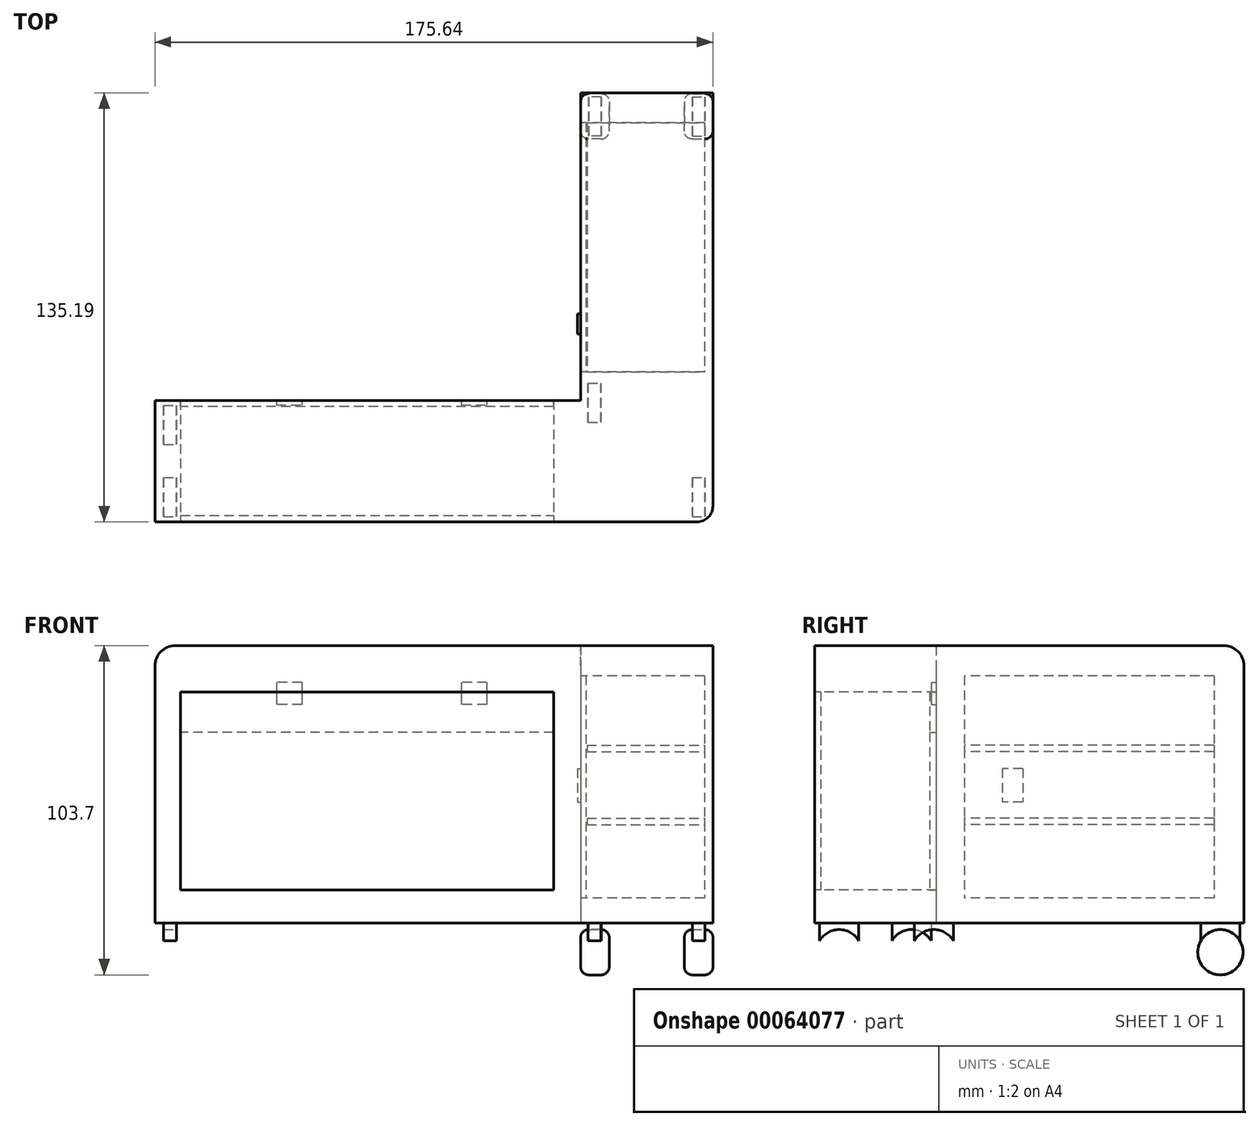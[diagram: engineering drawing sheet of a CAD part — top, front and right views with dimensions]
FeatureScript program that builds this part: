
annotation { "Feature Type Name" : "Feature", "Feature Type Description" : "" }
export const myFeature = defineFeature(function(context is Context, id is Id, definition is map)
    precondition{}
    {
        {
            var Q0;
            Q0=qCreatedBy(makeId("Front.planeOp"),FACE);
            var sketch = newSketch(context, id + "F0", { "sketchPlane" : qUnion([Q0])});
            skLineSegment(sketch, "E0.rect.bottom", {"start": v(-60.65, 49.22) * mm, "end": v(67, 49.22) * mm});
            skLineSegment(sketch, "E0.rect.left", {"start": v(-67, 42.87) * mm, "end": v(-67, -38.15) * mm});
            skLineSegment(sketch, "E0.rect.right", {"start": v(67, 49.22) * mm, "end": v(67, -38.15) * mm});
            skPoint(sketch, "E0.rect.middle", {"position": v(0, 0) * mm});
            skPoint(sketch, "E1.visualSharp", {"position": v(-67, 49.22) * mm});
            skArc(sketch, "E1.filletArc", {"start": v(-60.65, 49.22) * mm, "mid": v(-65.14, 47.36) * mm, "end": v(-67, 42.87) * mm});
            skLineSegment(sketch, "E2", {"start": v(-67, -38.15) * mm, "end": v(67, -38.15) * mm});
            skPoint(sketch, "E0.rect.top.start.orphan", {"position": v(-67, -49.22) * mm});
            skPoint(sketch, "E3.orphan", {"position": v(67, -49.22) * mm});
            skSolve(sketch);
        }
        {
            var Q0;
            Q0=makeQuery(id+"F0.imprint","IMPRINT",FACE,{"disambiguationData":[TD([[makeQuery(id+"F0.imprint","IMPRINT",EDGE,{"derivedFrom":sQuery(id+"F0.wireOp",EDGE,"E0.rect.bottom")}),-1.0]])]});
            extrude(context, id + "F1", {"entities" : qUnion([Q0]), "depth" : 38.28 * mm});
        }
        {
            var Q0;
            Q0=makeQuery(id+"F1.opExtrude","CAP_FACE",FACE,{"disambiguationData":[OSD([sQuery(id+"F0.wireOp",EDGE,"E0.rect.bottom"),sQuery(id+"F0.wireOp",EDGE,"E0.rect.left"),sQuery(id+"F0.wireOp",EDGE,"E0.rect.right"),sQuery(id+"F0.wireOp",EDGE,"E1.filletArc"),sQuery(id+"F0.wireOp",EDGE,"E2")])],"isStart":false});
            var sketch = newSketch(context, id + "F2", { "sketchPlane" : qUnion([Q0])});
            skLineSegment(sketch, "E4.bottom", {"start": v(-58.97, 34.69) * mm, "end": v(58.47, 34.69) * mm});
            skLineSegment(sketch, "E4.top", {"start": v(-58.97, -27.7) * mm, "end": v(58.47, -27.7) * mm});
            skLineSegment(sketch, "E4.left", {"start": v(-58.97, 34.69) * mm, "end": v(-58.97, -27.7) * mm});
            skLineSegment(sketch, "E4.right", {"start": v(58.47, 34.69) * mm, "end": v(58.47, -27.7) * mm});
            skSolve(sketch);
        }
        {
            var Q0;
            Q0=qSketchRegion(id+"F2",true);
            extrude(context, id + "F3", {"entities" : qUnion([Q0]), "operationType" : NewBodyOperationType.REMOVE, "endBound" : BoundingType.THROUGH_ALL, "oppositeDirection" : true, "depth" : 25 * mm});
        }
        {
            var Q0;
            Q0=makeQuery(id+"F1.opExtrude","CAP_FACE",FACE,{"disambiguationData":[OSD([sQuery(id+"F0.wireOp",EDGE,"E0.rect.bottom"),sQuery(id+"F0.wireOp",EDGE,"E0.rect.left"),sQuery(id+"F0.wireOp",EDGE,"E0.rect.right"),sQuery(id+"F0.wireOp",EDGE,"E1.filletArc"),sQuery(id+"F0.wireOp",EDGE,"E2")])],"isStart":false});
            var sketch = newSketch(context, id + "F4", { "sketchPlane" : qUnion([Q0])});
            skLineSegment(sketch, "E5.0", {"start": v(-58.97, 34.69) * mm, "end": v(58.47, 34.69) * mm});
            skLineSegment(sketch, "E6.0", {"start": v(-58.97, 34.69) * mm, "end": v(-58.97, -27.7) * mm});
            skLineSegment(sketch, "E7.0", {"start": v(-58.97, -27.7) * mm, "end": v(58.47, -27.7) * mm});
            skLineSegment(sketch, "E8.0", {"start": v(58.47, 34.69) * mm, "end": v(58.47, -27.7) * mm});
            skSolve(sketch);
        }
        {
            var Q0;
            Q0=makeQuery(id+"F4.imprint","IMPRINT",FACE,{"disambiguationData":[TD([[makeQuery(id+"F4.imprint","IMPRINT",EDGE,{"derivedFrom":sQuery(id+"F4.wireOp",EDGE,"E5.0")}),-1.0]])]});
            extrude(context, id + "F5", {"entities" : qUnion([Q0]), "oppositeDirection" : true, "depth" : 2 * mm});
        }
        {
            var Q0;
            Q0=makeQuery(id+"F1.opExtrude","CAP_FACE",FACE,{"disambiguationData":[OSD([sQuery(id+"F0.wireOp",EDGE,"E0.rect.bottom"),sQuery(id+"F0.wireOp",EDGE,"E0.rect.left"),sQuery(id+"F0.wireOp",EDGE,"E0.rect.right"),sQuery(id+"F0.wireOp",EDGE,"E1.filletArc"),sQuery(id+"F0.wireOp",EDGE,"E2")])],"isStart":true});
            var sketch = newSketch(context, id + "F6", { "sketchPlane" : qUnion([Q0])});
            skLineSegment(sketch, "E9.0", {"start": v(-58.47, 21.87) * mm, "end": v(-58.47, -27.7) * mm});
            skLineSegment(sketch, "E10.0", {"start": v(58.97, -27.7) * mm, "end": v(-58.47, -27.7) * mm});
            skLineSegment(sketch, "E11.0", {"start": v(58.97, 21.87) * mm, "end": v(58.97, -27.7) * mm});
            skLineSegment(sketch, "E12", {"start": v(-58.47, 21.87) * mm, "end": v(58.97, 21.87) * mm});
            skPoint(sketch, "E13.0.end.orphan", {"position": v(-58.47, 34.69) * mm});
            skPoint(sketch, "E14.orphan", {"position": v(58.97, 34.69) * mm});
            skSolve(sketch);
        }
        {
            var Q0;
            Q0=makeQuery(id+"F6.imprint","IMPRINT",FACE,{"disambiguationData":[TD([[makeQuery(id+"F6.imprint","IMPRINT",EDGE,{"derivedFrom":sQuery(id+"F6.wireOp",EDGE,"E9.0")}),1.0]])]});
            extrude(context, id + "F7", {"entities" : qUnion([Q0]), "oppositeDirection" : true, "depth" : 2 * mm});
        }
        {
            var Q0;
            Q0=makeQuery(id+"F1.opExtrude","CAP_FACE",FACE,{"disambiguationData":[OSD([sQuery(id+"F0.wireOp",EDGE,"E0.rect.bottom"),sQuery(id+"F0.wireOp",EDGE,"E0.rect.left"),sQuery(id+"F0.wireOp",EDGE,"E0.rect.right"),sQuery(id+"F0.wireOp",EDGE,"E1.filletArc"),sQuery(id+"F0.wireOp",EDGE,"E2")])],"isStart":true});
            var sketch = newSketch(context, id + "F8", { "sketchPlane" : qUnion([Q0])});
            skLineSegment(sketch, "E15.0", {"start": v(58.97, 34.69) * mm, "end": v(-58.47, 34.69) * mm});
            skLineSegment(sketch, "E16.0", {"start": v(-58.47, 34.69) * mm, "end": v(-58.47, 21.87) * mm});
            skLineSegment(sketch, "E17.0", {"start": v(-58.47, 21.87) * mm, "end": v(58.97, 21.87) * mm});
            skLineSegment(sketch, "E18.0", {"start": v(58.97, 34.69) * mm, "end": v(58.97, 21.87) * mm});
            skPoint(sketch, "E19.orphan", {"position": v(-58.47, -27.7) * mm});
            skPoint(sketch, "E20.orphan", {"position": v(58.97, -27.7) * mm});
            skSolve(sketch);
        }
        {
            var Q0;
            Q0=makeQuery(id+"F8.imprint","IMPRINT",FACE,{"disambiguationData":[TD([[makeQuery(id+"F8.imprint","IMPRINT",EDGE,{"derivedFrom":sQuery(id+"F8.wireOp",EDGE,"E15.0")}),1.0]])]});
            extrude(context, id + "F9", {"entities" : qUnion([Q0]), "oppositeDirection" : true, "depth" : 2 * mm});
        }
        {
            var Q0;
            Q0=makeQuery(id+"F1.opExtrude","CAP_FACE",FACE,{"disambiguationData":[OSD([sQuery(id+"F0.wireOp",EDGE,"E0.rect.bottom"),sQuery(id+"F0.wireOp",EDGE,"E0.rect.left"),sQuery(id+"F0.wireOp",EDGE,"E0.rect.right"),sQuery(id+"F0.wireOp",EDGE,"E1.filletArc"),sQuery(id+"F0.wireOp",EDGE,"E2")])],"isStart":true});
            cPlane(context, id + "F10", {"entities" : qUnion([Q0]), "cplaneType" : CPlaneType.OFFSET, "offset" : 0 * mm, "width" : 150 * mm, "height" : 150 * mm});
        }
        {
            var Q0;
            Q0=qCreatedBy(id+"F10.planeOp",FACE);
            var sketch = newSketch(context, id + "F11", { "sketchPlane" : qUnion([Q0])});
            skLineSegment(sketch, "E21.bottom", {"start": v(-37.46, 37.7) * mm, "end": v(-29.46, 37.7) * mm});
            skLineSegment(sketch, "E21.top", {"start": v(-37.46, 30.7) * mm, "end": v(-29.46, 30.7) * mm});
            skLineSegment(sketch, "E21.left", {"start": v(-37.46, 37.7) * mm, "end": v(-37.46, 30.7) * mm});
            skLineSegment(sketch, "E21.right", {"start": v(-29.46, 37.7) * mm, "end": v(-29.46, 30.7) * mm});
            skPoint(sketch, "E22.firstSnap0", {"position": v(-33.46, 37.7) * mm});
            skLineSegment(sketch, "E22.bottom", {"start": v(20.75, 37.7) * mm, "end": v(28.75, 37.7) * mm});
            skLineSegment(sketch, "E22.top", {"start": v(20.75, 30.7) * mm, "end": v(28.75, 30.7) * mm});
            skLineSegment(sketch, "E22.left", {"start": v(20.75, 37.7) * mm, "end": v(20.75, 30.7) * mm});
            skLineSegment(sketch, "E22.right", {"start": v(28.75, 37.7) * mm, "end": v(28.75, 30.7) * mm});
            skSolve(sketch);
        }
        {
            var Q0;
            Q0=makeQuery(id+"F11.imprint","IMPRINT",FACE,{"disambiguationData":[TD([[makeQuery(id+"F11.imprint","IMPRINT",EDGE,{"derivedFrom":sQuery(id+"F11.wireOp",EDGE,"E21.bottom")}),-1.0]])]});
            var Q1;
            Q1=makeQuery(id+"F11.imprint","IMPRINT",FACE,{"disambiguationData":[TD([[makeQuery(id+"F11.imprint","IMPRINT",EDGE,{"derivedFrom":sQuery(id+"F11.wireOp",EDGE,"E22.bottom")}),-1.0]])]});
            extrude(context, id + "F12", {"entities" : qUnion([Q0, Q1]), "operationType" : NewBodyOperationType.REMOVE, "oppositeDirection" : true, "depth" : 1.5 * mm});
        }
        {
            var Q0;
            Q0=qCreatedBy(id+"F10.planeOp",FACE);
            var sketch = newSketch(context, id + "F13", { "sketchPlane" : qUnion([Q0])});
            skLineSegment(sketch, "E23.0", {"start": v(-37.46, 37.7) * mm, "end": v(-29.46, 37.7) * mm});
            skLineSegment(sketch, "E24.0", {"start": v(-37.46, 37.7) * mm, "end": v(-37.46, 34.69) * mm});
            skLineSegment(sketch, "E25.0", {"start": v(-37.46, 34.69) * mm, "end": v(-37.46, 30.7) * mm});
            skLineSegment(sketch, "E26.0", {"start": v(-37.46, 30.7) * mm, "end": v(-29.46, 30.7) * mm});
            skLineSegment(sketch, "E27.0", {"start": v(-29.46, 34.69) * mm, "end": v(-29.46, 30.7) * mm});
            skLineSegment(sketch, "E28.0", {"start": v(-29.46, 37.7) * mm, "end": v(-29.46, 34.69) * mm});
            skLineSegment(sketch, "E29.0", {"start": v(20.75, 37.7) * mm, "end": v(20.75, 34.69) * mm});
            skLineSegment(sketch, "E30.0", {"start": v(20.75, 37.7) * mm, "end": v(28.75, 37.7) * mm});
            skLineSegment(sketch, "E31.0", {"start": v(28.75, 37.7) * mm, "end": v(28.75, 34.69) * mm});
            skLineSegment(sketch, "E32.0", {"start": v(28.75, 34.69) * mm, "end": v(28.75, 30.7) * mm});
            skLineSegment(sketch, "E33.0", {"start": v(20.75, 30.7) * mm, "end": v(28.75, 30.7) * mm});
            skLineSegment(sketch, "E34.0.0", {"start": v(20.75, 34.69) * mm, "end": v(20.75, 30.7) * mm});
            skLineSegment(sketch, "E34.0.2", {"start": v(28.75, 30.7) * mm, "end": v(28.75, 34.69) * mm});
            skSolve(sketch);
        }
        {
            var Q0;
            Q0=makeQuery(id+"F13.imprint","IMPRINT",FACE,{"disambiguationData":[TD([[makeQuery(id+"F13.imprint","IMPRINT",EDGE,{"derivedFrom":sQuery(id+"F13.wireOp",EDGE,"E23.0")}),-1.0]])]});
            var Q1;
            Q1=makeQuery(id+"F13.imprint","IMPRINT",FACE,{"disambiguationData":[TD([[makeQuery(id+"F13.imprint","IMPRINT",EDGE,{"derivedFrom":sQuery(id+"F13.wireOp",EDGE,"E29.0")}),1.0]])]});
            extrude(context, id + "F14", {"entities" : qUnion([Q0, Q1]), "oppositeDirection" : true, "depth" : 1.5 * mm});
        }
        {
            var Q0;
            Q0=makeQuery(id+"F1.opExtrude","SWEPT_FACE",FACE,{"disambiguationData":[OSD([sQuery(id+"F0.wireOp",EDGE,"E0.rect.right")])]});
            cPlane(context, id + "F15", {"entities" : qUnion([Q0]), "cplaneType" : CPlaneType.OFFSET, "offset" : 0 * mm, "width" : 150 * mm, "height" : 150 * mm});
        }
        {
            var Q0;
            Q0=qCreatedBy(id+"F15.planeOp",FACE);
            var sketch = newSketch(context, id + "F16", { "sketchPlane" : qUnion([Q0])});
            skLineSegment(sketch, "E35.0", {"start": v(-38.28, 49.22) * mm, "end": v(0, 49.22) * mm});
            skLineSegment(sketch, "E36.0", {"start": v(-38.28, 49.22) * mm, "end": v(-38.28, -38.15) * mm});
            skLineSegment(sketch, "E37.0", {"start": v(-38.28, -38.15) * mm, "end": v(0, -38.15) * mm});
            skLineSegment(sketch, "E38", {"start": v(0, 49.22) * mm, "end": v(90.56, 49.22) * mm});
            skLineSegment(sketch, "E39", {"start": v(96.9, -38.15) * mm, "end": v(0, -38.15) * mm});
            skLineSegment(sketch, "E40", {"start": v(96.9, 42.87) * mm, "end": v(96.9, -38.15) * mm});
            skPoint(sketch, "E41.visualSharp", {"position": v(96.9, 49.22) * mm});
            skArc(sketch, "E41.filletArc", {"start": v(96.9, 42.87) * mm, "mid": v(95.05, 47.36) * mm, "end": v(90.56, 49.22) * mm});
            skSolve(sketch);
        }
        {
            var Q0;
            Q0=makeQuery(id+"F16.imprint","IMPRINT",FACE,{"disambiguationData":[TD([[makeQuery(id+"F16.imprint","IMPRINT",EDGE,{"derivedFrom":sQuery(id+"F16.wireOp",EDGE,"E35.0")}),-1.0]])]});
            extrude(context, id + "F17", {"entities" : qUnion([Q0]), "operationType" : NewBodyOperationType.ADD, "depth" : 41.64 * mm});
        }
        {
            var Q0;
            Q0=makeQuery(id+"F17.opExtrude","CAP_EDGE",EDGE,{"disambiguationData":[OSD([sQuery(id+"F16.wireOp",EDGE,"E36.0")])],"isStart":false});
            fillet(context, id + "F18", {"entities" : qUnion([Q0]), "radius" : 5 * mm, "tangentPropagation" : true, "allowEdgeOverflow" : false});
        }
        {
            var Q0;
            Q0=makeQuery(id+"F17.opExtrude","CAP_FACE",FACE,{"disambiguationData":[OSD([sQuery(id+"F16.wireOp",EDGE,"E35.0"),sQuery(id+"F16.wireOp",EDGE,"E36.0"),sQuery(id+"F16.wireOp",EDGE,"E37.0"),sQuery(id+"F16.wireOp",EDGE,"E38"),sQuery(id+"F16.wireOp",EDGE,"E39"),sQuery(id+"F16.wireOp",EDGE,"E40"),sQuery(id+"F16.wireOp",EDGE,"E41.filletArc")])],"isStart":true});
            var sketch = newSketch(context, id + "F19", { "sketchPlane" : qUnion([Q0])});
            skLineSegment(sketch, "E42.bottom", {"start": v(-87.48, 39.73) * mm, "end": v(-8.92, 39.73) * mm});
            skLineSegment(sketch, "E42.top", {"start": v(-87.48, -30.33) * mm, "end": v(-8.92, -30.33) * mm});
            skLineSegment(sketch, "E42.left", {"start": v(-87.48, 39.73) * mm, "end": v(-87.48, -30.33) * mm});
            skLineSegment(sketch, "E42.right", {"start": v(-8.92, 39.73) * mm, "end": v(-8.92, -30.33) * mm});
            skSolve(sketch);
        }
        {
            var Q0;
            Q0=qSketchRegion(id+"F19",true);
            extrude(context, id + "F20", {"entities" : qUnion([Q0]), "operationType" : NewBodyOperationType.REMOVE, "oppositeDirection" : true, "depth" : 39 * mm});
        }
        {
            var Q0;
            Q0=makeQuery(id+"F20.boolean.opBoolean","COPY",FACE,{"derivedFrom":makeQuery(id+"F20.opExtrude","CAP_FACE",FACE,{"disambiguationData":[OSD([sQuery(id+"F19.wireOp",EDGE,"E42.bottom"),sQuery(id+"F19.wireOp",EDGE,"E42.top"),sQuery(id+"F19.wireOp",EDGE,"E42.left"),sQuery(id+"F19.wireOp",EDGE,"E42.right")])],"isStart":false})});
            var sketch = newSketch(context, id + "F21", { "sketchPlane" : qUnion([Q0])});
            skLineSegment(sketch, "E43.rect.left", {"start": v(-87.48, 15.81) * mm, "end": v(-87.48, 17.81) * mm});
            skLineSegment(sketch, "E43.rect.right", {"start": v(-8.92, 15.81) * mm, "end": v(-8.92, 17.81) * mm});
            skPoint(sketch, "E43.rect.middle", {"position": v(-48.2, 16.81) * mm});
            skLineSegment(sketch, "E44.rect.left", {"start": v(-87.48, -5.19) * mm, "end": v(-87.48, -7.19) * mm});
            skLineSegment(sketch, "E44.rect.right", {"start": v(-8.92, -5.19) * mm, "end": v(-8.92, -7.19) * mm});
            skPoint(sketch, "E44.rect.middle", {"position": v(-48.2, -6.19) * mm});
            skPoint(sketch, "E45.orphan", {"position": v(-87.48, -6.19) * mm});
            skPoint(sketch, "E46.end.orphan", {"position": v(-8.92, -6.19) * mm});
            skPoint(sketch, "E47.orphan", {"position": v(-87.48, 16.81) * mm});
            skPoint(sketch, "E48.end.orphan", {"position": v(-8.92, 16.81) * mm});
            skLineSegment(sketch, "E49", {"start": v(-8.92, 17.81) * mm, "end": v(-8.92, 15.81) * mm});
            skLineSegment(sketch, "E50", {"start": v(-87.48, 17.81) * mm, "end": v(-87.48, 15.81) * mm});
            skLineSegment(sketch, "E51.bottom", {"start": v(-87.48, 17.81) * mm, "end": v(-8.92, 17.81) * mm});
            skLineSegment(sketch, "E51.top", {"start": v(-87.48, 15.81) * mm, "end": v(-8.92, 15.81) * mm});
            skLineSegment(sketch, "E51.left", {"start": v(-87.48, 17.81) * mm, "end": v(-87.48, 16.81) * mm});
            skLineSegment(sketch, "E52.bottom", {"start": v(-87.48, -5.19) * mm, "end": v(-8.92, -5.19) * mm});
            skLineSegment(sketch, "E52.top", {"start": v(-87.48, -7.19) * mm, "end": v(-8.92, -7.19) * mm});
            skSolve(sketch);
        }
        {
            var Q0;
            {var subQ0=sQuery(id+"F21.wireOp",EDGE,"E51.bottom");Q0=makeQuery(id+"F21.imprint","IMPRINT",FACE,{"disambiguationData":[TD([[makeQuery(id+"F21.imprint","IMPRINT",EDGE,{"derivedFrom":subQ0}),-1.0]])]});}
            var Q1;
            Q1=makeQuery(id+"F21.imprint","IMPRINT",FACE,{"disambiguationData":[TD([[makeQuery(id+"F21.imprint","IMPRINT",EDGE,{"derivedFrom":sQuery(id+"F21.wireOp",EDGE,"E52.bottom")}),-1.0]])]});
            extrude(context, id + "F22", {"entities" : qUnion([Q0, Q1]), "depth" : 37 * mm});
        }
        {
            var Q0;
            Q0=makeQuery(id+"F17.opExtrude","CAP_FACE",FACE,{"disambiguationData":[OSD([sQuery(id+"F16.wireOp",EDGE,"E35.0"),sQuery(id+"F16.wireOp",EDGE,"E36.0"),sQuery(id+"F16.wireOp",EDGE,"E37.0"),sQuery(id+"F16.wireOp",EDGE,"E38"),sQuery(id+"F16.wireOp",EDGE,"E39"),sQuery(id+"F16.wireOp",EDGE,"E40"),sQuery(id+"F16.wireOp",EDGE,"E41.filletArc")])],"isStart":true});
            var sketch = newSketch(context, id + "F23", { "sketchPlane" : qUnion([Q0])});
            skLineSegment(sketch, "E53.0", {"start": v(-87.48, 39.73) * mm, "end": v(-8.92, 39.73) * mm});
            skLineSegment(sketch, "E54.0", {"start": v(-87.48, 39.73) * mm, "end": v(-87.48, -30.33) * mm});
            skLineSegment(sketch, "E55.0", {"start": v(-87.48, -30.33) * mm, "end": v(-8.92, -30.33) * mm});
            skLineSegment(sketch, "E56.0", {"start": v(-8.92, 39.73) * mm, "end": v(-8.92, -30.33) * mm});
            skSolve(sketch);
        }
        {
            var Q0;
            Q0=qSketchRegion(id+"F23",true);
            extrude(context, id + "F24", {"entities" : qUnion([Q0]), "oppositeDirection" : true, "depth" : 1.72 * mm});
        }
        {
            var Q0;
            Q0=makeQuery(id+"F24.opExtrude","CAP_FACE",FACE,{"disambiguationData":[OSD([sQuery(id+"F23.wireOp",EDGE,"E53.0"),sQuery(id+"F23.wireOp",EDGE,"E54.0"),sQuery(id+"F23.wireOp",EDGE,"E55.0"),sQuery(id+"F23.wireOp",EDGE,"E56.0")])],"isStart":true});
            var sketch = newSketch(context, id + "F25", { "sketchPlane" : qUnion([Q0])});
            skLineSegment(sketch, "E57.bottom", {"start": v(-27.26, 10.52) * mm, "end": v(-20.85, 10.52) * mm});
            skLineSegment(sketch, "E57.top", {"start": v(-27.26, 0) * mm, "end": v(-20.85, 0) * mm});
            skLineSegment(sketch, "E57.left", {"start": v(-27.26, 10.52) * mm, "end": v(-27.26, 0) * mm});
            skLineSegment(sketch, "E57.right", {"start": v(-20.85, 10.52) * mm, "end": v(-20.85, 0) * mm});
            skSolve(sketch);
        }
        {
            var Q0;
            Q0=qSketchRegion(id+"F25",true);
            extrude(context, id + "F26", {"entities" : qUnion([Q0]), "operationType" : NewBodyOperationType.ADD, "depth" : 1 * mm});
        }
        {
            var Q0;
            Q0=makeQuery(id+"F17.opExtrude","CAP_FACE",FACE,{"disambiguationData":[OSD([sQuery(id+"F16.wireOp",EDGE,"E35.0"),sQuery(id+"F16.wireOp",EDGE,"E36.0"),sQuery(id+"F16.wireOp",EDGE,"E37.0"),sQuery(id+"F16.wireOp",EDGE,"E38"),sQuery(id+"F16.wireOp",EDGE,"E39"),sQuery(id+"F16.wireOp",EDGE,"E40"),sQuery(id+"F16.wireOp",EDGE,"E41.filletArc")])],"isStart":false});
            var sketch = newSketch(context, id + "F27", { "sketchPlane" : qUnion([Q0])});
            skCircle(sketch, "E58", {"center": v(89.48, -47.35) * mm, "radius": 7.14 * mm});
            skSolve(sketch);
        }
        {
            var Q0;
            Q0=makeQuery(id+"F27.imprint","IMPRINT",FACE,{"disambiguationData":[TD([[makeQuery(id+"F27.imprint","IMPRINT",EDGE,{"derivedFrom":sQuery(id+"F27.wireOp",EDGE,"E58")}),1.0]])]});
            extrude(context, id + "F28", {"entities" : qUnion([Q0]), "oppositeDirection" : true, "depth" : 9 * mm});
        }
        {
            var Q0;
            Q0=makeQuery(id+"F28.opExtrude","CAP_EDGE",EDGE,{"disambiguationData":[OSD([sQuery(id+"F27.wireOp",EDGE,"E58")])],"isStart":true});
            var Q1;
            Q1=makeQuery(id+"F28.opExtrude","CAP_EDGE",EDGE,{"disambiguationData":[OSD([sQuery(id+"F27.wireOp",EDGE,"E58")])],"isStart":false});
            fillet(context, id + "F29", {"entities" : qUnion([Q0, Q1]), "radius" : 2.5 * mm, "tangentPropagation" : true, "allowEdgeOverflow" : false});
        }
        {
            var Q0;
            Q0=makeQuery(id+"F28.opExtrude","CAP_FACE",FACE,{"disambiguationData":[OSD([sQuery(id+"F27.wireOp",EDGE,"E58")])],"isStart":true});
            cPlane(context, id + "F30", {"entities" : qUnion([Q0]), "cplaneType" : CPlaneType.OFFSET, "offset" : 2.5 * mm, "oppositeDirection" : true, "width" : 150 * mm, "height" : 150 * mm});
        }
        {
            var Q0;
            Q0=qCreatedBy(id+"F30.planeOp",FACE);
            var sketch = newSketch(context, id + "F31", { "sketchPlane" : qUnion([Q0])});
            skArc(sketch, "E59.0", {"start": v(95.63, -43.73) * mm, "mid": v(89.48, -40.2) * mm, "end": v(83.32, -43.73) * mm});
            skLineSegment(sketch, "E60.0", {"start": v(83.32, -38.15) * mm, "end": v(95.63, -38.15) * mm});
            skLineSegment(sketch, "E61", {"start": v(83.32, -38.15) * mm, "end": v(83.32, -43.73) * mm});
            skLineSegment(sketch, "E62", {"start": v(95.63, -43.73) * mm, "end": v(95.63, -38.15) * mm});
            skPoint(sketch, "E63.orphan", {"position": v(-33.28, -38.15) * mm});
            skPoint(sketch, "E64.orphan", {"position": v(96.9, -38.15) * mm});
            skSolve(sketch);
        }
        {
            var Q0;
            Q0=makeQuery(id+"F31.imprint","IMPRINT",FACE,{"disambiguationData":[TD([[makeQuery(id+"F31.imprint","IMPRINT",EDGE,{"derivedFrom":sQuery(id+"F31.wireOp",EDGE,"E59.0")}),-1.0]])]});
            extrude(context, id + "F32", {"entities" : qUnion([Q0]), "oppositeDirection" : true, "depth" : 4 * mm});
        }
        {
            var Q0;
            Q0=makeQuery(id+"F17.opExtrude","SWEPT_FACE",FACE,{"disambiguationData":[OSD([sQuery(id+"F16.wireOp",EDGE,"E40")])]});
            var sketch = newSketch(context, id + "F33", { "sketchPlane" : qUnion([Q0])});
            skLineSegment(sketch, "E65.0", {"start": v(-108.64, -38.15) * mm, "end": v(-67, -38.15) * mm, "construction": true});
            skLineSegment(sketch, "E66", {"start": v(-87.82, -38.15) * mm, "end": v(-87.82, 27.49) * mm, "construction": true});
            skSolve(sketch);
        }
        {
            var Q0;
            Q0=sQuery(id+"F33.wireOp",EDGE,"E66");
            cPlane(context, id + "F34", {"entities" : qUnion([Q0]), "cplaneType" : CPlaneType.LINE_ANGLE, "offset" : 150 * mm, "angle" : 0 * degree, "width" : 150 * mm, "height" : 150 * mm});
        }
        {
            var Q0;
            Q0=makeQuery(id+"F28.opExtrude","SWEPT_BODY",BODY,{"disambiguationData":[OSD([sQuery(id+"F27.wireOp",EDGE,"E58")])]});
            var Q1;
            Q1=makeQuery(id+"F32.opExtrude","SWEPT_BODY",BODY,{"disambiguationData":[OSD([sQuery(id+"F31.wireOp",EDGE,"E59.0"),sQuery(id+"F31.wireOp",EDGE,"E60.0"),sQuery(id+"F31.wireOp",EDGE,"E61"),sQuery(id+"F31.wireOp",EDGE,"E62")])]});
            var Q2;
            Q2=qCreatedBy(id+"F34.planeOp",FACE);
            mirror(context, id + "F35", {"entities" : qUnion([Q0, Q1]), "mirrorPlane" : qUnion([Q2])});
        }
        {
            var Q0;
            Q0=makeQuery(id+"F32.opExtrude","SWEPT_BODY",BODY,{"disambiguationData":[OSD([sQuery(id+"F31.wireOp",EDGE,"E59.0"),sQuery(id+"F31.wireOp",EDGE,"E60.0"),sQuery(id+"F31.wireOp",EDGE,"E61"),sQuery(id+"F31.wireOp",EDGE,"E62")])]});
            transform(context, id + "F36", {"entities" : qUnion([Q0]), "transformType" : TransformType.TRANSLATION_3D, "dx" : 0 * mm, "dy" : -120 * mm, "dz" : 0 * mm, "makeCopy" : true});
        }
        {
            var Q0;
            Q0=makeQuery(id+"F36.opPattern","COPY",BODY,{"derivedFrom":makeQuery(id+"F32.opExtrude","SWEPT_BODY",BODY,{"disambiguationData":[OSD([sQuery(id+"F31.wireOp",EDGE,"E59.0"),sQuery(id+"F31.wireOp",EDGE,"E60.0"),sQuery(id+"F31.wireOp",EDGE,"E61"),sQuery(id+"F31.wireOp",EDGE,"E62")])]}),"instanceName":"1"});
            transform(context, id + "F37", {"entities" : qUnion([Q0]), "transformType" : TransformType.TRANSLATION_3D, "dx" : -166.4 * mm, "dy" : 0 * mm, "dz" : 0 * mm, "makeCopy" : true});
        }
        {
            var Q0;
            Q0=makeQuery(id+"F1.opExtrude","SWEPT_FACE",FACE,{"disambiguationData":[OSD([sQuery(id+"F0.wireOp",EDGE,"E0.rect.left")])]});
            var sketch = newSketch(context, id + "F38", { "sketchPlane" : qUnion([Q0])});
            skLineSegment(sketch, "E67.0", {"start": v(38.28, -38.15) * mm, "end": v(0, -38.15) * mm, "construction": true});
            skLineSegment(sketch, "E68", {"start": v(19.14, -38.15) * mm, "end": v(19.14, 29.3) * mm, "construction": true});
            skSolve(sketch);
        }
        {
            var Q0;
            Q0=sQuery(id+"F38.wireOp",EDGE,"E68");
            cPlane(context, id + "F39", {"entities" : qUnion([Q0]), "cplaneType" : CPlaneType.LINE_ANGLE, "offset" : 150 * mm, "angle" : 90 * degree, "width" : 150 * mm, "height" : 150 * mm});
        }
        {
            var Q0;
            Q0=makeQuery(id+"F37.opPattern","COPY",BODY,{"derivedFrom":makeQuery(id+"F36.opPattern","COPY",BODY,{"derivedFrom":makeQuery(id+"F32.opExtrude","SWEPT_BODY",BODY,{"disambiguationData":[OSD([sQuery(id+"F31.wireOp",EDGE,"E59.0"),sQuery(id+"F31.wireOp",EDGE,"E60.0"),sQuery(id+"F31.wireOp",EDGE,"E61"),sQuery(id+"F31.wireOp",EDGE,"E62")])]}),"instanceName":"1"}),"instanceName":"1"});
            var Q1;
            Q1=qCreatedBy(id+"F39.planeOp",FACE);
            mirror(context, id + "F40", {"entities" : qUnion([Q0]), "mirrorPlane" : qUnion([Q1])});
        }
        {
            var Q0;
            Q0=makeQuery(id+"F40.opPattern","COPY",BODY,{"derivedFrom":makeQuery(id+"F37.opPattern","COPY",BODY,{"derivedFrom":makeQuery(id+"F36.opPattern","COPY",BODY,{"derivedFrom":makeQuery(id+"F32.opExtrude","SWEPT_BODY",BODY,{"disambiguationData":[OSD([sQuery(id+"F31.wireOp",EDGE,"E59.0"),sQuery(id+"F31.wireOp",EDGE,"E60.0"),sQuery(id+"F31.wireOp",EDGE,"E61"),sQuery(id+"F31.wireOp",EDGE,"E62")])]}),"instanceName":"1"}),"instanceName":"1"}),"instanceName":"1"});
            transform(context, id + "F41", {"entities" : qUnion([Q0]), "transformType" : TransformType.TRANSLATION_3D, "dx" : 133.58 * mm, "dy" : 7.02 * mm, "dz" : 0 * mm, "makeCopy" : true});
        }
    });
